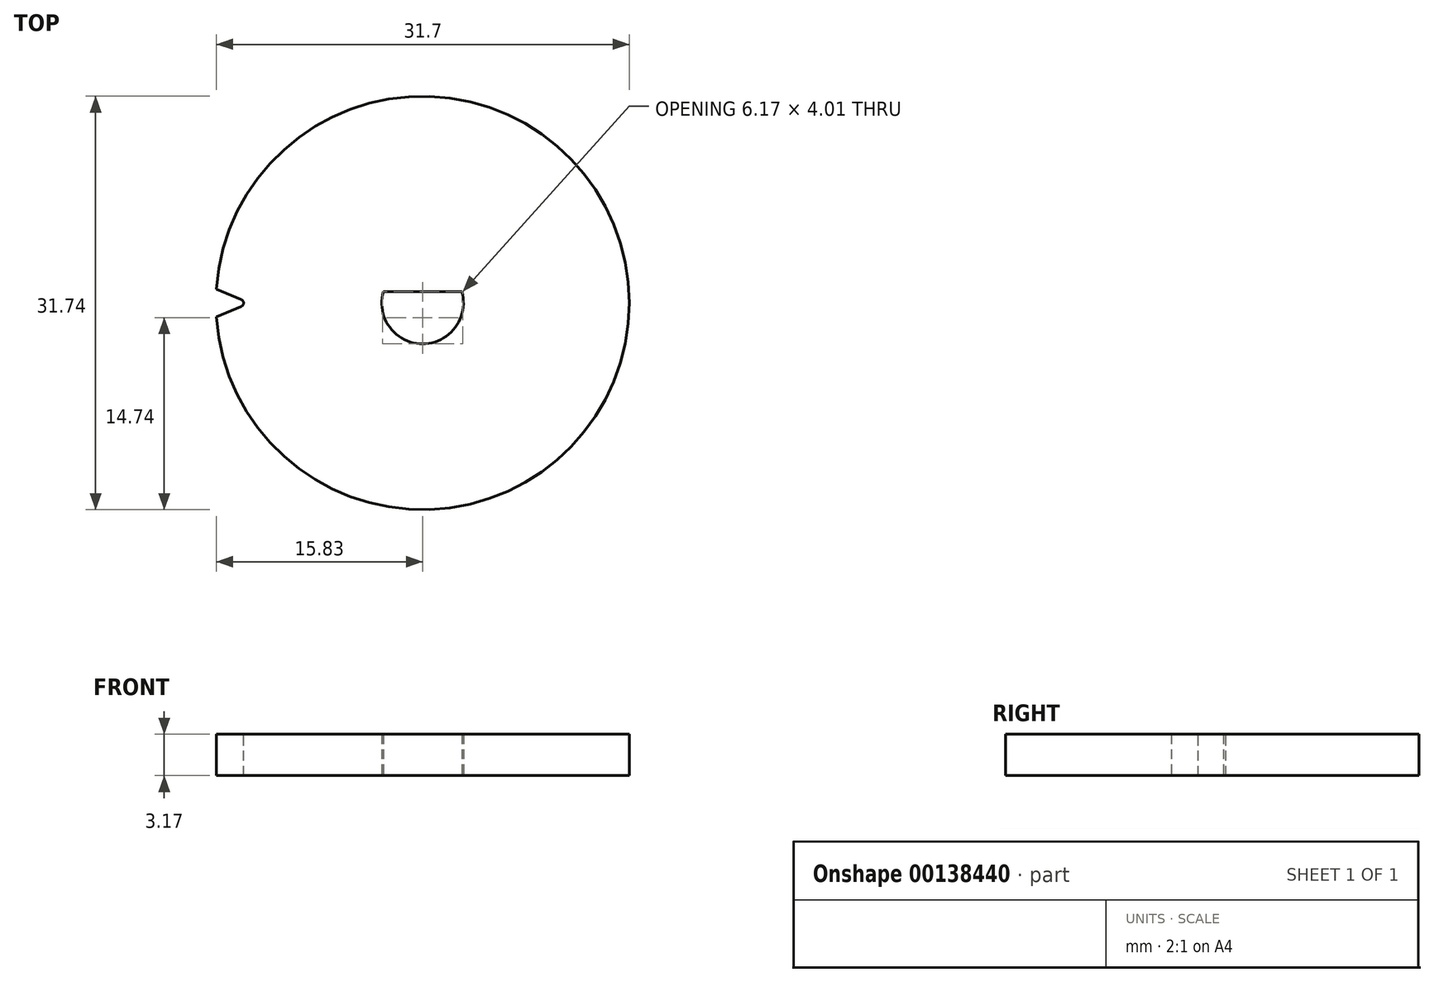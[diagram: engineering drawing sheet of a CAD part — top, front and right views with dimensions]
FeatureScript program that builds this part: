
annotation { "Feature Type Name" : "Feature", "Feature Type Description" : "" }
export const myFeature = defineFeature(function(context is Context, id is Id, definition is map)
    precondition{}
    {
        {
            var Q0;
            Q0=qCreatedBy(makeId("Top.planeOp"),FACE);
            var sketch = newSketch(context, id + "F0", { "sketchPlane" : qUnion([Q0])});
            skCircle(sketch, "E0", {"center": v(0, 0) * mm, "radius": 15.87 * mm});
            skArc(sketch, "E1", {"start": v(-3.01, 0.88) * mm, "mid": v(0, -3.14) * mm, "end": v(3.01, 0.88) * mm});
            skLineSegment(sketch, "E2", {"start": v(0, 0) * mm, "end": v(0, 0.88) * mm, "construction": true});
            skLineSegment(sketch, "E3", {"start": v(-3.01, 0.88) * mm, "end": v(3.01, 0.88) * mm});
            skSolve(sketch);
        }
        {
            var Q0;
            Q0=qSketchRegion(id+"F0",true);
            extrude(context, id + "F1", {"entities" : qUnion([Q0]), "depth" : 3.17 * mm});
        }
        {
            var Q0;
            Q0=makeQuery(id+"F1.opExtrude","CAP_FACE",FACE,{"disambiguationData":[OSD([sQuery(id+"F0.wireOp",EDGE,"E0"),sQuery(id+"F0.wireOp",EDGE,"Ac06N18u-JPQ2-7IZA-F2du-Al0p21rmLt66"),sQuery(id+"F0.wireOp",EDGE,"6mnEyKxW-Fp10-a9Po-mJho-hWrt6oDyfDzS"),sQuery(id+"F0.wireOp",EDGE,"2ctZUJaF-SXab-fNJr-841c-qtTdgy4iuLxU")])],"isStart":false});
            var sketch = newSketch(context, id + "F2", { "sketchPlane" : qUnion([Q0])});
            skLineSegment(sketch, "E4", {"start": v(0, 0) * mm, "end": v(-15.87, 0) * mm, "construction": true});
            skLineSegment(sketch, "E5", {"start": v(0, 0) * mm, "end": v(-15.85, 0.71) * mm, "construction": true});
            skArc(sketch, "E6", {"start": v(-15.83, 1.07) * mm, "mid": v(-15.87, 0) * mm, "end": v(-15.83, -1.07) * mm});
            skArc(sketch, "E7", {"start": v(-13.93, -0.27) * mm, "mid": v(-13.75, 0) * mm, "end": v(-13.93, 0.27) * mm});
            skLineSegment(sketch, "E8", {"start": v(-15.83, -1.07) * mm, "end": v(-13.93, -0.27) * mm});
            skLineSegment(sketch, "E9", {"start": v(-13.93, 0.27) * mm, "end": v(-15.83, 1.07) * mm});
            skPoint(sketch, "E10", {"position": v(-14.88, 0.67) * mm});
            skSolve(sketch);
        }
        {
            var Q0;
            Q0=qSketchRegion(id+"F2",true);
            var Q1;
            Q1=makeQuery(id+"F1.opExtrude","CAP_FACE",FACE,{"disambiguationData":[OSD([sQuery(id+"F0.wireOp",EDGE,"E0"),sQuery(id+"F0.wireOp",EDGE,"Ac06N18u-JPQ2-7IZA-F2du-Al0p21rmLt66"),sQuery(id+"F0.wireOp",EDGE,"6mnEyKxW-Fp10-a9Po-mJho-hWrt6oDyfDzS"),sQuery(id+"F0.wireOp",EDGE,"2ctZUJaF-SXab-fNJr-841c-qtTdgy4iuLxU")])],"isStart":true});
            extrude(context, id + "F3", {"entities" : qUnion([Q0]), "operationType" : NewBodyOperationType.REMOVE, "endBound" : BoundingType.UP_TO_SURFACE, "oppositeDirection" : true, "endBoundEntityFace" : qUnion([Q1]), "depth" : 25.4 * mm});
        }
    });
